# Revit family: FU_Chair_Sandler_Woodlook 2-5
name_source: partatom
category: Furniture
units: mm (PartAtom-declared; Revit-internal decimal feet)

## family parameters
Always vertical = Yes
Cut with Voids When Loaded = No
OmniClass Number = 23.40.20.00
OmniClass Title = General Furniture and Specialties
Room Calculation Point = No
Shared = No
Work Plane-Based = No

## types (1)
- FU_Chair_Sandler_Woodlook 2-5
    Arm Height = 680 mm  [stored 2.23097 ft]
    Default Elevation = 0 mm  [stored 0 ft]
    Depth = 515 mm  [stored 1.68963 ft]
    Description = Woodlook armchair with frame manufactured entirely from aluminum but with realistic appearance of wood. Highly durable and scratch resistant.
    Height = 855 mm  [stored 2.80512 ft]
    Manufacturer = Sandler
    Model = Woodlook 2.5
    Overall width = 595 mm  [stored 1.9521 ft]
    URL = https://www.sandlerseating.com
    Upholstery = Fabric - Mainline Flax - Upminster MLF20
    Width = 490 mm  [stored 1.60761 ft]
    Woodlook = Woodlook - 21A Teak

note: [stored X ft] marks values corroborated as IEEE doubles in the binary element streams (Revit-internal decimal feet)

## geometry (parser evidence)
native form markers: Sweep x3
no freeform markers — native parametric forms only
